# Revit family: Bolzenanker BZ plus, vz
name_source: partatom
category: HLS-Bauteile
revit_build: Autodesk Revit 2018 (Build: 20190510_1515(x64)
units: mm (PartAtom-declared; Revit-internal decimal feet)

## family parameters
Basisbauteil = Fläche
Beim Laden mit Abzugskörper schneiden = Nein
Bemaßung runder Anschluss = Durchmesser verwenden
Gemeinsam genutzt = Ja
Raumberechnungspunkt = Nein
Teiletyp = Normal

## types (12) — shared parameters
Fabrikat = MKT
Firma = MEFA Befestigungs- und Montagesysteme GmbH
Kurztext1 = Bolzenanker BZ plus
Material = Stahl
Mengeneinheit = St
Vorgabe-Ansicht = 1219 mm

## per-type parameters (varying)
| type | Artikelnummer | Bohrlochtiefe | Bohrlochtiefe red. | D | EAN | Gewicht | Gewicht pro Bauteil | Gewinde | Kurztext2 | L | L1 | L2 | Länge Dübel | Länge Gewinde | Mutter | Setztiefe | Setztiefe red. | Unterlegscheibe | Verankerungstiefe | Verankerungstiefe red. | max. Klemmstärke red. | vpe |
| BZ+  8- 10- 21/ 75, vz | 221108010 | 60 mm | 49 mm | 7 mm  [stored 0.0229659 ft] | 4043315045379 | 0.03 kg | 0.03 kg | M8 | Länge Gewinde 32 mm Stahl | 75 mm | 60 mm | 15 mm  [stored 0.0492126 ft] | 75 mm | 32 mm  [stored 0.104987 ft] | Sechskantmutter : Sechskantmutter M8 | 52 mm | 41 mm | Unterlegscheibe : Unterlegscheibe 8.4x16x1.6 | 46 mm | 35 mm | 21 mm | 100 St |
| BZ+ 10- 50- 70/130, vz | 221110050 | 75 mm | 55 mm | 8 mm  [stored 0.0262467 ft] | 4043315045478 | 0.08 kg | 0.08 kg | M10 | Länge Gewinde 82 mm Stahl | 130 mm | 115 mm | 15 mm  [stored 0.0492126 ft] | 130 mm | 82 mm | Sechskantmutter : Sechskantmutter M10 | 68 mm | 48 mm | Unterlegscheibe : Unterlegscheibe 10.5x20x2 | 60 mm | 40 mm | 70 mm | 50 St |
| BZ+  8- 30- 41/ 95, vz | 221108030 | 60 mm | 49 mm | 7 mm  [stored 0.0229659 ft] | 4043315045393 | 0.04 kg | 0.04 kg | M8 | Länge Gewinde 52 mm Stahl | 95 mm | 80 mm | 15 mm  [stored 0.0492126 ft] | 95 mm | 52 mm | Sechskantmutter : Sechskantmutter M8 | 52 mm | 41 mm | Unterlegscheibe : Unterlegscheibe 8.4x16x1.6 | 46 mm | 35 mm | 41 mm | 100 St |
| BZ+ 10- 10- 30/ 90, vz | 221110010 | 75 mm | 55 mm | 8 mm  [stored 0.0262467 ft] | 4043315045423 | 0.06 kg | 0.06 kg | M10 | Länge Gewinde 42 mm Stahl | 90 mm | 75 mm | 15 mm  [stored 0.0492126 ft] | 90 mm | 42 mm | Sechskantmutter : Sechskantmutter M10 | 68 mm | 48 mm | Unterlegscheibe : Unterlegscheibe 10.5x20x2 | 60 mm | 40 mm | 30 mm | 50 St |
| BZ+ 10- 30- 50/110, vz | 221110030 | 75 mm | 55 mm | 8 mm  [stored 0.0262467 ft] | 4043315045461 | 0.07 kg | 0.07 kg | M10 | Länge Gewinde 62 mm Stahl | 110 mm | 95 mm | 15 mm  [stored 0.0492126 ft] | 110 mm | 62 mm | Sechskantmutter : Sechskantmutter M10 | 68 mm | 48 mm | Unterlegscheibe : Unterlegscheibe 10.5x20x2 | 60 mm | 40 mm | 50 mm | 50 St |
| BZ+ 12- 15- 35/110, vz | 221112015 | 90 mm | 70 mm | 10 mm  [stored 0.0328084 ft] | 4043315096432 | 0.10 kg | 0.10 kg | M12 | Länge Gewinde 51 mm Stahl | 110 mm | 95 mm | 15 mm  [stored 0.0492126 ft] | 110 mm | 51 mm | Sechskantmutter : Sechskantmutter M12 | 80 mm | 60 mm | Unterlegscheibe : Unterlegscheibe 13x24x2.5 | 70 mm | 50 mm | 35 mm | 25 St |
| BZ+ 12- 30- 50/125, vz | 22111203001 | 90 mm | 70 mm | 10 mm  [stored 0.0328084 ft] | 4043315096814 | 0.11 kg | 0.11 kg | M12 | Länge Gewinde 66 mm Stahl | 125 mm | 110 mm | 15 mm  [stored 0.0492126 ft] | 125 mm | 66 mm | Sechskantmutter : Sechskantmutter M12 | 80 mm | 60 mm | Unterlegscheibe : Unterlegscheibe 13x24x2.5 | 70 mm | 50 mm | 50 mm | 25 St |
| BZ+ 12- 50- 70/145, vz | 221112050 | 90 mm | 70 mm | 10 mm  [stored 0.0328084 ft] | 4043315096869 | 0.13 kg | 0.13 kg | M12 | Länge Gewinde 86 mm Stahl | 145 mm | 130 mm | 15 mm  [stored 0.0492126 ft] | 145 mm | 86 mm | Sechskantmutter : Sechskantmutter M12 | 80 mm | 60 mm | Unterlegscheibe : Unterlegscheibe 13x24x2.5 | 70 mm | 50 mm | 70 mm | 25 St |
| BZ+ 12-105-125/200, vz | 221112105 | 90 mm | 70 mm | 10 mm  [stored 0.0328084 ft] | 4043315096487 | 0.17 kg | 0.17 kg | M12 | Länge Gewinde 141 mm Stahl | 200 mm  [stored 0.656168 ft] | 180 mm  [stored 0.590551 ft] | 20 mm  [stored 0.0656168 ft] | 200 mm  [stored 0.656168 ft] | 141 mm | Sechskantmutter : Sechskantmutter M12 | 80 mm | 60 mm | Unterlegscheibe : Unterlegscheibe 13x24x2.5 | 70 mm | 50 mm | 125 mm | 25 St |
| BZ+ 16- 15- 35/135, vz | 221116015 | 110 mm | 90 mm | 14 mm  [stored 0.0459318 ft] | 4043315045119 | 0.22 kg | 0.22 kg | M16 | Länge Gewinde 56 mm Stahl | 135 mm  [stored 0.442913 ft] | 115 mm | 20 mm  [stored 0.0656168 ft] | 135 mm  [stored 0.442913 ft] | 56 mm | Sechskantmutter : Sechskantmutter M16 | 97 mm | 77 mm | Unterlegscheibe : Unterlegscheibe, verstärkt 17x44x3.5 | 85 mm | 65 mm | 35 mm | 20 St |
| BZ+ 16- 25- 45/145, vz | 221116025 | 110 mm | 90 mm | 14 mm  [stored 0.0459318 ft] | 4043315045126 | 0.23 kg | 0.23 kg | M16 | Länge Gewinde 66 mm Stahl | 145 mm | 125 mm | 20 mm  [stored 0.0656168 ft] | 145 mm | 66 mm | Sechskantmutter : Sechskantmutter M16 | 97 mm | 77 mm | Unterlegscheibe : Unterlegscheibe, verstärkt 17x44x3.5 | 85 mm | 65 mm | 45 mm | 20 St |
| BZ+ 16- 80-100/200, vz | 221116080 | 110 mm | 90 mm | 14 mm  [stored 0.0459318 ft] | 4250928449290 | 0.32 kg | 0.32 kg | M16 | Länge Gewinde 121 mm Stahl | 200 mm  [stored 0.656168 ft] | 180 mm  [stored 0.590551 ft] | 20 mm  [stored 0.0656168 ft] | 200 mm  [stored 0.656168 ft] | 121 mm | Sechskantmutter : Sechskantmutter M16 | 97 mm | 77 mm | Unterlegscheibe : Unterlegscheibe, verstärkt 17x44x3.5 | 85 mm | 65 mm | 100 mm | 10 St |

note: [stored X ft] marks values corroborated as IEEE doubles in the binary element streams (Revit-internal decimal feet)

## geometry (parser evidence)
native form markers: Sweep x3
no freeform markers — native parametric forms only
